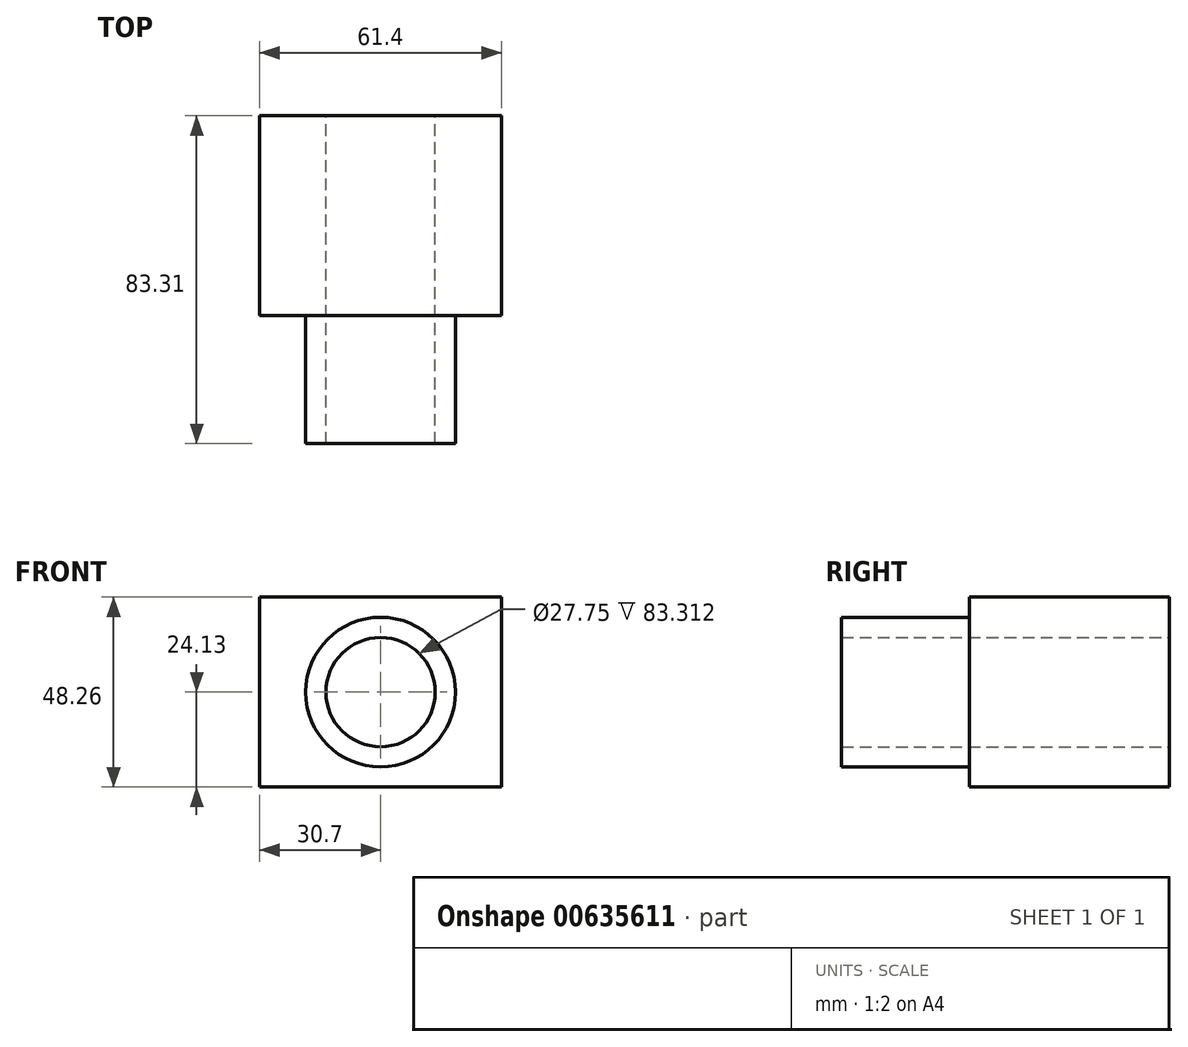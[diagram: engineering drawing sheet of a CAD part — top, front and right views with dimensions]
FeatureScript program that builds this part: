
annotation { "Feature Type Name" : "Feature", "Feature Type Description" : "" }
export const myFeature = defineFeature(function(context is Context, id is Id, definition is map)
    precondition{}
    {
        {
            var Q0;
            Q0=qCreatedBy(makeId("Front.planeOp"),FACE);
            var sketch = newSketch(context, id + "F0", { "sketchPlane" : qUnion([Q0])});
            skLineSegment(sketch, "E0.bottom", {"start": v(30.7, 24.13) * mm, "end": v(-30.7, 24.13) * mm});
            skLineSegment(sketch, "E0.top", {"start": v(30.7, -24.13) * mm, "end": v(-30.7, -24.13) * mm});
            skLineSegment(sketch, "E0.left", {"start": v(30.7, 24.13) * mm, "end": v(30.7, -24.13) * mm});
            skLineSegment(sketch, "E0.right", {"start": v(-30.7, 24.13) * mm, "end": v(-30.7, -24.13) * mm});
            skPoint(sketch, "E0.middle", {"position": v(0, 0) * mm});
            skCircle(sketch, "E1", {"center": v(0, 0) * mm, "radius": 19.02 * mm});
            skCircle(sketch, "E2", {"center": v(0, 0) * mm, "radius": 13.87 * mm});
            skSolve(sketch);
        }
        {
            var Q0;
            Q0 = qSketchRegion(id + "F0", true);
            extrude(context, id + "F1", {"entities" : qUnion([Q0]), "depth" : 50.8 * mm, "offsetDistance" : 25.4 * mm});
        }
        {
            var Q0;
            Q0=makeQuery(id+"F0.imprint","IMPRINT",FACE,{"disambiguationData":[TD([[makeQuery(id+"F0.imprint","IMPRINT",EDGE,{"derivedFrom":sQuery(id+"F0.wireOp",EDGE,"E1")}),1.0]])]});
            extrude(context, id + "F2", {"entities" : qUnion([Q0]), "operationType" : NewBodyOperationType.ADD, "depth" : 83.31 * mm, "offsetDistance" : 25.4 * mm});
        }
    });
